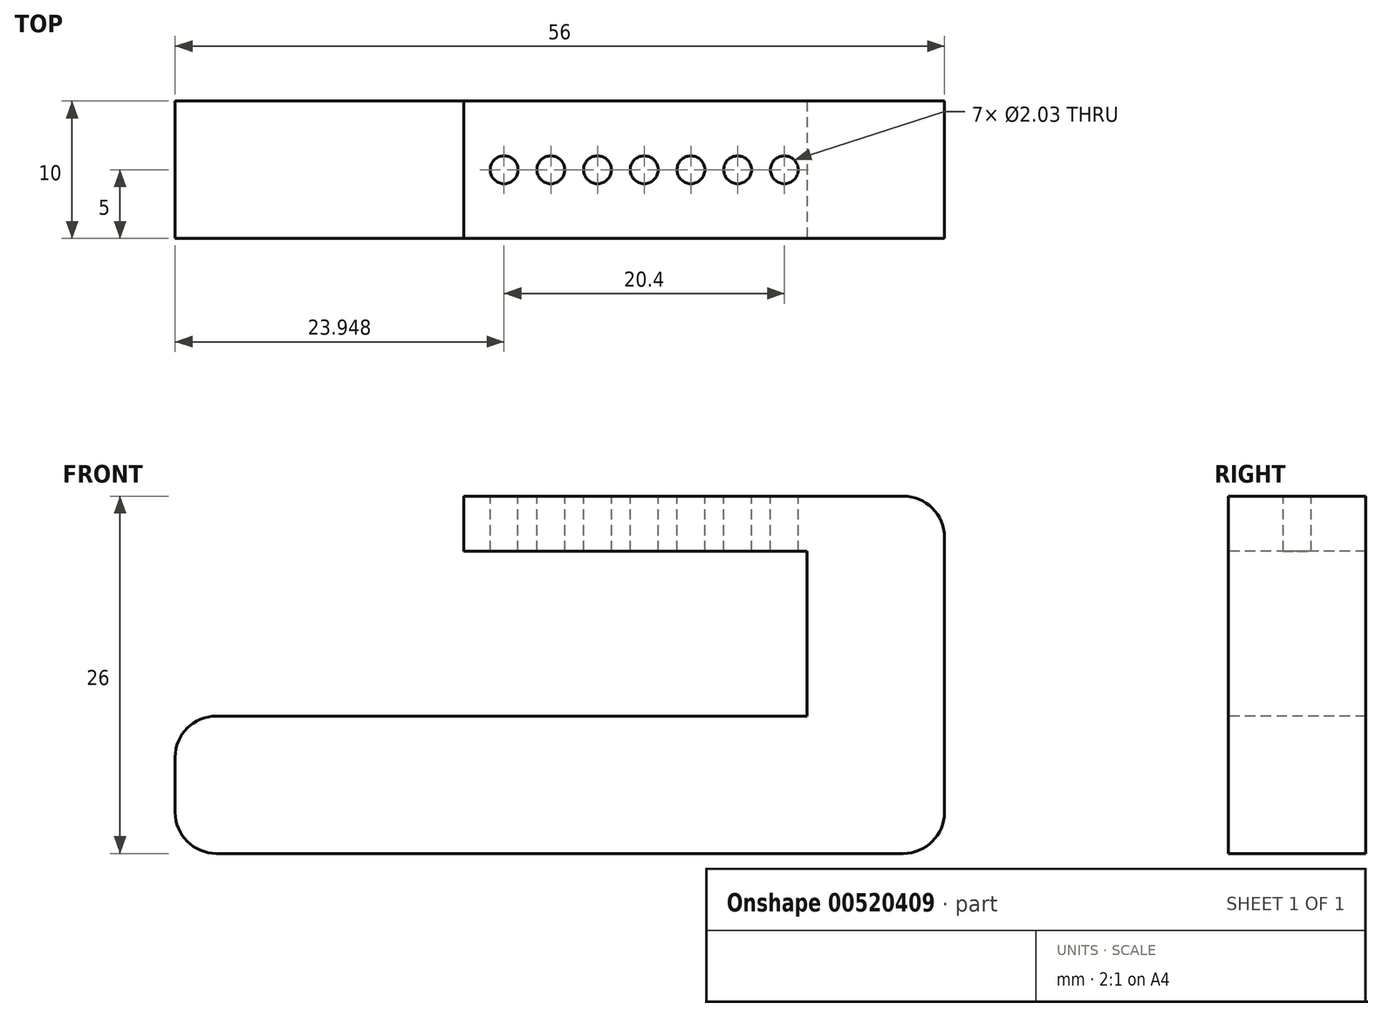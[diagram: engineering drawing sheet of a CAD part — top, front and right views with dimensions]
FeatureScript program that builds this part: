
annotation { "Feature Type Name" : "Feature", "Feature Type Description" : "" }
export const myFeature = defineFeature(function(context is Context, id is Id, definition is map)
    precondition{}
    {
        {
            var Q0;
            Q0=qCreatedBy(makeId("Top.planeOp"),FACE);
            var sketch = newSketch(context, id + "F0", { "sketchPlane" : qUnion([Q0])});
            skLineSegment(sketch, "E0.bottom", {"start": v(-28, 5) * mm, "end": v(28, 5) * mm});
            skLineSegment(sketch, "E0.top", {"start": v(-28, -5) * mm, "end": v(28, -5) * mm});
            skLineSegment(sketch, "E0.left", {"start": v(-28, 5) * mm, "end": v(-28, -5) * mm});
            skLineSegment(sketch, "E0.right", {"start": v(28, 5) * mm, "end": v(28, -5) * mm});
            skSolve(sketch);
        }
        {
            var Q0;
            Q0 = qSketchRegion(id + "F0", true);
            extrude(context, id + "F1", {"entities" : qUnion([Q0]), "depth" : 1.8 * mm, "offsetDistance" : 25 * mm});
        }
        {
            var Q0;
            Q0=makeQuery(id+"F1.opExtrude","SWEPT_EDGE",EDGE,{"disambiguationData":[OSD([sQuery(id+"F0.wireOp",EDGE,"E0.bottom"),sQuery(id+"F0.wireOp",EDGE,"E0.left")])]});
            var Q1;
            Q1=makeQuery(id+"F1.opExtrude","SWEPT_EDGE",EDGE,{"disambiguationData":[OSD([sQuery(id+"F0.wireOp",EDGE,"E0.bottom"),sQuery(id+"F0.wireOp",EDGE,"E0.right")])]});
            var Q2;
            Q2=makeQuery(id+"F1.opExtrude","SWEPT_EDGE",EDGE,{"disambiguationData":[OSD([sQuery(id+"F0.wireOp",EDGE,"E0.top"),sQuery(id+"F0.wireOp",EDGE,"E0.right")])]});
            var Q3;
            Q3=makeQuery(id+"F1.opExtrude","SWEPT_EDGE",EDGE,{"disambiguationData":[OSD([sQuery(id+"F0.wireOp",EDGE,"E0.top"),sQuery(id+"F0.wireOp",EDGE,"E0.left")])]});
            fillet(context, id + "F2", {"entities" : qUnion([Q0, Q1, Q2, Q3]), "radius" : 3 * mm, "tangentPropagation" : true, "allowEdgeOverflow" : false});
        }
        {
            var Q0;
            Q0 = qSketchRegion(id + "F0", true);
            extrude(context, id + "F3", {"entities" : qUnion([Q0]), "operationType" : NewBodyOperationType.ADD, "depth" : 10 * mm, "offsetDistance" : 25 * mm});
        }
        {
            var Q0;
            Q0=makeQuery(id+"F3.opExtrude","CAP_FACE",FACE,{"disambiguationData":[OSD([sQuery(id+"F0.wireOp",EDGE,"E0.bottom"),sQuery(id+"F0.wireOp",EDGE,"E0.top"),sQuery(id+"F0.wireOp",EDGE,"E0.left"),sQuery(id+"F0.wireOp",EDGE,"E0.right")])],"isStart":false});
            var sketch = newSketch(context, id + "F4", { "sketchPlane" : qUnion([Q0])});
            skLineSegment(sketch, "E1.0.0", {"start": v(-28, 5) * mm, "end": v(-28, -5) * mm});
            skLineSegment(sketch, "E1.0.1", {"start": v(-28, -5) * mm, "end": v(28, -5) * mm});
            skLineSegment(sketch, "E1.0.2", {"start": v(28, -5) * mm, "end": v(28, 5) * mm});
            skLineSegment(sketch, "E1.0.3", {"start": v(28, 5) * mm, "end": v(-28, 5) * mm});
            skLineSegment(sketch, "E2", {"start": v(18, 5) * mm, "end": v(18, -5) * mm});
            skSolve(sketch);
        }
        {
            var Q0;
            {var subQ0=sQuery(id+"F4.wireOp",EDGE,"E1.0.2");Q0=makeQuery(id+"F4.imprint","IMPRINT",FACE,{"disambiguationData":[TD([[makeQuery(id+"F4.imprint","IMPRINT",EDGE,{"derivedFrom":subQ0}),-1.0]])]});}
            extrude(context, id + "F5", {"entities" : qUnion([Q0]), "operationType" : NewBodyOperationType.ADD, "depth" : 16 * mm, "offsetDistance" : 25 * mm});
        }
        {
            var Q0;
            Q0=makeQuery(id+"F5.opExtrude","SWEPT_FACE",FACE,{"disambiguationData":[OSD([sQuery(id+"F4.wireOp",EDGE,"E2")])]});
            var sketch = newSketch(context, id + "F6", { "sketchPlane" : qUnion([Q0])});
            skLineSegment(sketch, "E3.0.0", {"start": v(-5, 10) * mm, "end": v(5, 10) * mm});
            skLineSegment(sketch, "E3.0.1", {"start": v(5, 10) * mm, "end": v(5, 26) * mm});
            skLineSegment(sketch, "E3.0.2", {"start": v(5, 26) * mm, "end": v(-5, 26) * mm});
            skLineSegment(sketch, "E3.0.3", {"start": v(-5, 26) * mm, "end": v(-5, 10) * mm});
            skLineSegment(sketch, "E4", {"start": v(-5, 22) * mm, "end": v(5, 22) * mm});
            skSolve(sketch);
        }
        {
            var Q0;
            {var subQ0=sQuery(id+"F6.wireOp",EDGE,"E3.0.2");Q0=makeQuery(id+"F6.imprint","IMPRINT",FACE,{"disambiguationData":[TD([[makeQuery(id+"F6.imprint","IMPRINT",EDGE,{"derivedFrom":subQ0}),-1.0]])]});}
            extrude(context, id + "F7", {"entities" : qUnion([Q0]), "operationType" : NewBodyOperationType.ADD, "depth" : 25 * mm, "offsetDistance" : 25 * mm});
        }
        {
            var Q0;
            Q0=makeQuery(id+"F7.boolean.opBoolean","MERGE",FACE,{"derivedFrom":[makeQuery(id+"F5.opExtrude","CAP_FACE",FACE,{"disambiguationData":[OSD([sQuery(id+"F4.wireOp",EDGE,"E1.0.1"),sQuery(id+"F4.wireOp",EDGE,"E1.0.2"),sQuery(id+"F4.wireOp",EDGE,"E1.0.3"),sQuery(id+"F4.wireOp",EDGE,"E2")])],"isStart":false}),makeQuery(id+"F7.opExtrude","SWEPT_FACE",FACE,{"disambiguationData":[OSD([sQuery(id+"F6.wireOp",EDGE,"E3.0.2")])]})]});
            var sketch = newSketch(context, id + "F8", { "sketchPlane" : qUnion([Q0])});
            skLineSegment(sketch, "E5.0.0", {"start": v(28, 5) * mm, "end": v(-7, 5) * mm});
            skLineSegment(sketch, "E5.0.1", {"start": v(-7, 5) * mm, "end": v(-7, -5) * mm});
            skLineSegment(sketch, "E5.0.2", {"start": v(-7, -5) * mm, "end": v(28, -5) * mm});
            skLineSegment(sketch, "E5.0.3", {"start": v(28, -5) * mm, "end": v(28, 5) * mm});
            skLineSegment(sketch, "E6", {"start": v(-7, 0) * mm, "end": v(28, 0) * mm, "construction": true});
            skCircle(sketch, "E7", {"center": v(-4.05, 0) * mm, "radius": 1.01 * mm});
            skCircle(sketch, "E8.1.0.0", {"center": v(-0.65, 0) * mm, "radius": 1.01 * mm});
            skCircle(sketch, "E8.2.0.0", {"center": v(2.75, 0) * mm, "radius": 1.01 * mm});
            skCircle(sketch, "E8.3.0.0", {"center": v(6.15, 0) * mm, "radius": 1.01 * mm});
            skCircle(sketch, "E8.4.0.0", {"center": v(9.55, 0) * mm, "radius": 1.01 * mm});
            skCircle(sketch, "E8.5.0.0", {"center": v(12.95, 0) * mm, "radius": 1.01 * mm});
            skCircle(sketch, "E8.6.0.0", {"center": v(16.35, 0) * mm, "radius": 1.01 * mm});
            skLineSegment(sketch, "E8.direction1", {"start": v(-4.05, 0) * mm, "end": v(-0.65, 0) * mm, "construction": true});
            skSolve(sketch);
        }
        {
            var Q0;
            Q0=makeQuery(id+"F8.imprint","IMPRINT",FACE,{"disambiguationData":[TD([[makeQuery(id+"F8.imprint","IMPRINT",EDGE,{"derivedFrom":sQuery(id+"F8.wireOp",EDGE,"E7")}),1.0]])]});
            var Q1;
            Q1=makeQuery(id+"F8.imprint","IMPRINT",FACE,{"disambiguationData":[TD([[makeQuery(id+"F8.imprint","IMPRINT",EDGE,{"derivedFrom":sQuery(id+"F8.wireOp",EDGE,"E8.1.0.0")}),1.0]])]});
            var Q2;
            Q2=makeQuery(id+"F8.imprint","IMPRINT",FACE,{"disambiguationData":[TD([[makeQuery(id+"F8.imprint","IMPRINT",EDGE,{"derivedFrom":sQuery(id+"F8.wireOp",EDGE,"E8.2.0.0")}),1.0]])]});
            var Q3;
            Q3=makeQuery(id+"F8.imprint","IMPRINT",FACE,{"disambiguationData":[TD([[makeQuery(id+"F8.imprint","IMPRINT",EDGE,{"derivedFrom":sQuery(id+"F8.wireOp",EDGE,"E8.3.0.0")}),1.0]])]});
            var Q4;
            Q4=makeQuery(id+"F8.imprint","IMPRINT",FACE,{"disambiguationData":[TD([[makeQuery(id+"F8.imprint","IMPRINT",EDGE,{"derivedFrom":sQuery(id+"F8.wireOp",EDGE,"E8.4.0.0")}),1.0]])]});
            var Q5;
            Q5=makeQuery(id+"F8.imprint","IMPRINT",FACE,{"disambiguationData":[TD([[makeQuery(id+"F8.imprint","IMPRINT",EDGE,{"derivedFrom":sQuery(id+"F8.wireOp",EDGE,"E8.5.0.0")}),1.0]])]});
            var Q6;
            Q6=makeQuery(id+"F8.imprint","IMPRINT",FACE,{"disambiguationData":[TD([[makeQuery(id+"F8.imprint","IMPRINT",EDGE,{"derivedFrom":sQuery(id+"F8.wireOp",EDGE,"E8.6.0.0")}),1.0]])]});
            extrude(context, id + "F9", {"entities" : qUnion([Q0, Q1, Q2, Q3, Q4, Q5, Q6]), "operationType" : NewBodyOperationType.REMOVE, "oppositeDirection" : true, "depth" : 10 * mm, "offsetDistance" : 25 * mm});
        }
        {
            var Q0;
            Q0=makeQuery(id+"F5.opExtrude","CAP_EDGE",EDGE,{"disambiguationData":[OSD([sQuery(id+"F4.wireOp",EDGE,"E2")])],"isStart":true});
            var Q1;
            Q1=makeQuery(id+"F7.opExtrude","CAP_EDGE",EDGE,{"disambiguationData":[OSD([sQuery(id+"F6.wireOp",EDGE,"E4")])],"isStart":true});
            var Q2;
            Q2=makeQuery(id+"F5.opExtrude","CAP_EDGE",EDGE,{"disambiguationData":[OSD([sQuery(id+"F4.wireOp",EDGE,"E1.0.2")])],"isStart":false});
            var Q3;
            {var subQ0=sQuery(id+"F0.wireOp",EDGE,"E0.right");Q3=makeQuery(id+"F3.boolean.opBoolean","MERGE",EDGE,{"derivedFrom":[makeQuery(id+"F1.opExtrude","CAP_EDGE",EDGE,{"disambiguationData":[OSD([subQ0])],"isStart":true}),makeQuery(id+"F3.opExtrude","CAP_EDGE",EDGE,{"disambiguationData":[OSD([subQ0])],"isStart":true})]});}
            var Q4;
            {var subQ0=sQuery(id+"F0.wireOp",EDGE,"E0.left");Q4=makeQuery(id+"F3.boolean.opBoolean","MERGE",EDGE,{"derivedFrom":[makeQuery(id+"F1.opExtrude","CAP_EDGE",EDGE,{"disambiguationData":[OSD([subQ0])],"isStart":true}),makeQuery(id+"F3.opExtrude","CAP_EDGE",EDGE,{"disambiguationData":[OSD([subQ0])],"isStart":true})]});}
            var Q5;
            Q5=makeQuery(id+"F3.opExtrude","CAP_EDGE",EDGE,{"disambiguationData":[OSD([sQuery(id+"F0.wireOp",EDGE,"E0.left")])],"isStart":false});
            fillet(context, id + "F10", {"entities" : qUnion([Q0, Q1, Q2, Q3, Q4, Q5]), "radius" : 3 * mm, "tangentPropagation" : true, "allowEdgeOverflow" : false});
        }
    });
